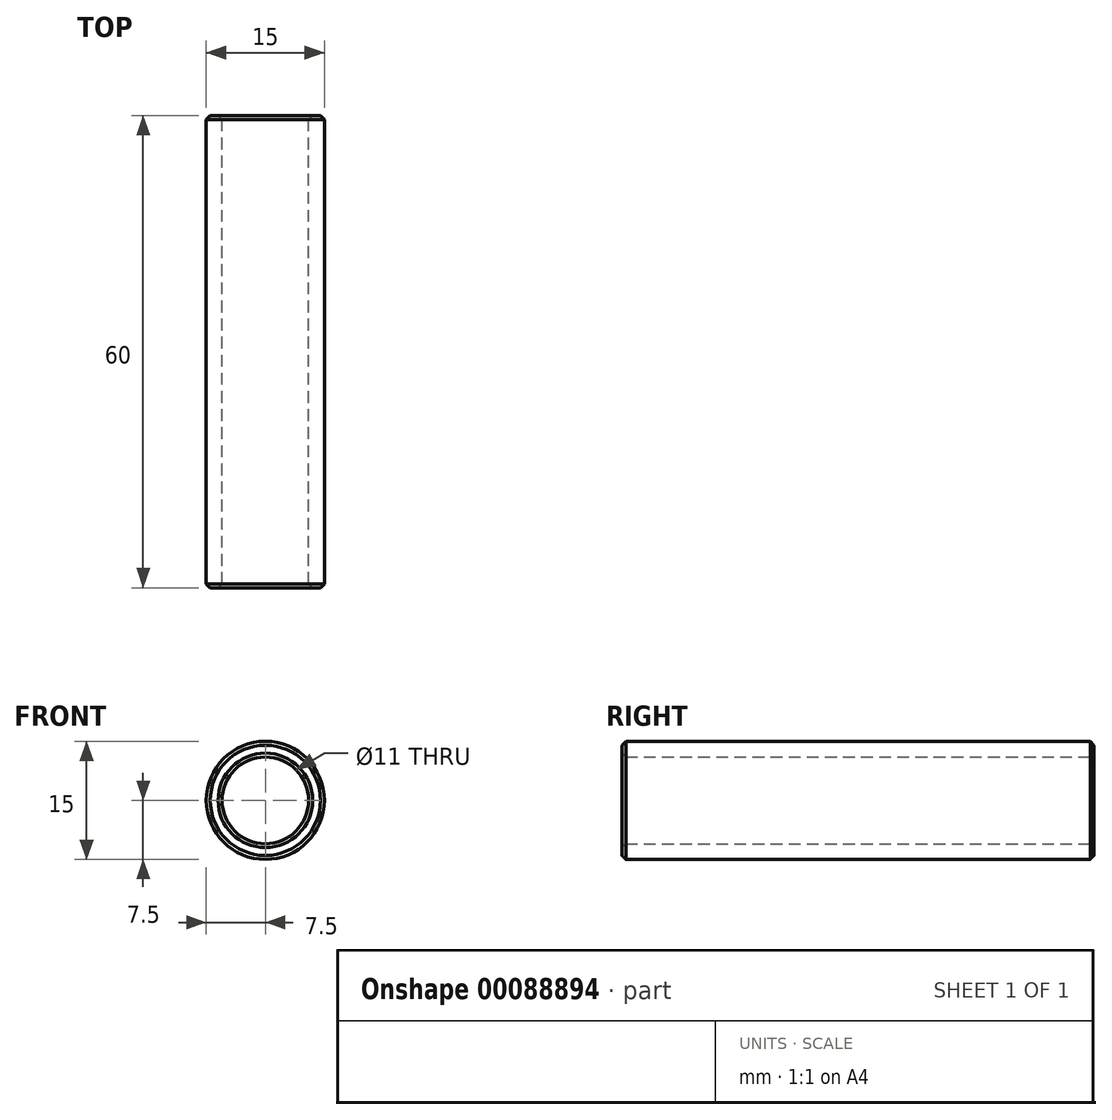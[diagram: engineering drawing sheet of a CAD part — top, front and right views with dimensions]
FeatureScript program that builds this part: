
annotation { "Feature Type Name" : "Feature", "Feature Type Description" : "" }
export const myFeature = defineFeature(function(context is Context, id is Id, definition is map)
    precondition{}
    {
        {
            var Q0;
            Q0=qCreatedBy(makeId("Front.planeOp"),FACE);
            var sketch = newSketch(context, id + "F0", { "sketchPlane" : qUnion([Q0])});
            skCircle(sketch, "E0", {"center": v(0, 0) * mm, "radius": 7.5 * mm});
            skCircle(sketch, "E1", {"center": v(0, 0) * mm, "radius": 5.5 * mm});
            skSolve(sketch);
        }
        {
            var Q0;
            Q0=makeQuery(id+"F0.imprint","IMPRINT",FACE,{"disambiguationData":[TD([[makeQuery(id+"F0.imprint","IMPRINT",EDGE,{"derivedFrom":sQuery(id+"F0.wireOp",EDGE,"E0")}),1.0]])]});
            extrude(context, id + "F1", {"entities" : qUnion([Q0]), "endBound" : BoundingType.SYMMETRIC, "depth" : 60 * mm});
        }
        {
            var Q0;
            Q0=makeQuery(id+"F1.opExtrude","CAP_EDGE",EDGE,{"disambiguationData":[OSD([sQuery(id+"F0.wireOp",EDGE,"E0")])],"isStart":false});
            var Q1;
            Q1=makeQuery(id+"F1.opExtrude","CAP_EDGE",EDGE,{"disambiguationData":[OSD([sQuery(id+"F0.wireOp",EDGE,"E0")])],"isStart":true});
            var Q2;
            Q2=makeQuery(id+"F1.opExtrude","CAP_EDGE",EDGE,{"disambiguationData":[OSD([sQuery(id+"F0.wireOp",EDGE,"E1")])],"isStart":false});
            var Q3;
            Q3=makeQuery(id+"F1.opExtrude","CAP_EDGE",EDGE,{"disambiguationData":[OSD([sQuery(id+"F0.wireOp",EDGE,"E1")])],"isStart":true});
            chamfer(context, id + "F2", {"entities" : qUnion([Q0, Q1, Q2, Q3]), "width" : .5 * mm, "tangentPropagation" : true});
        }
    });
